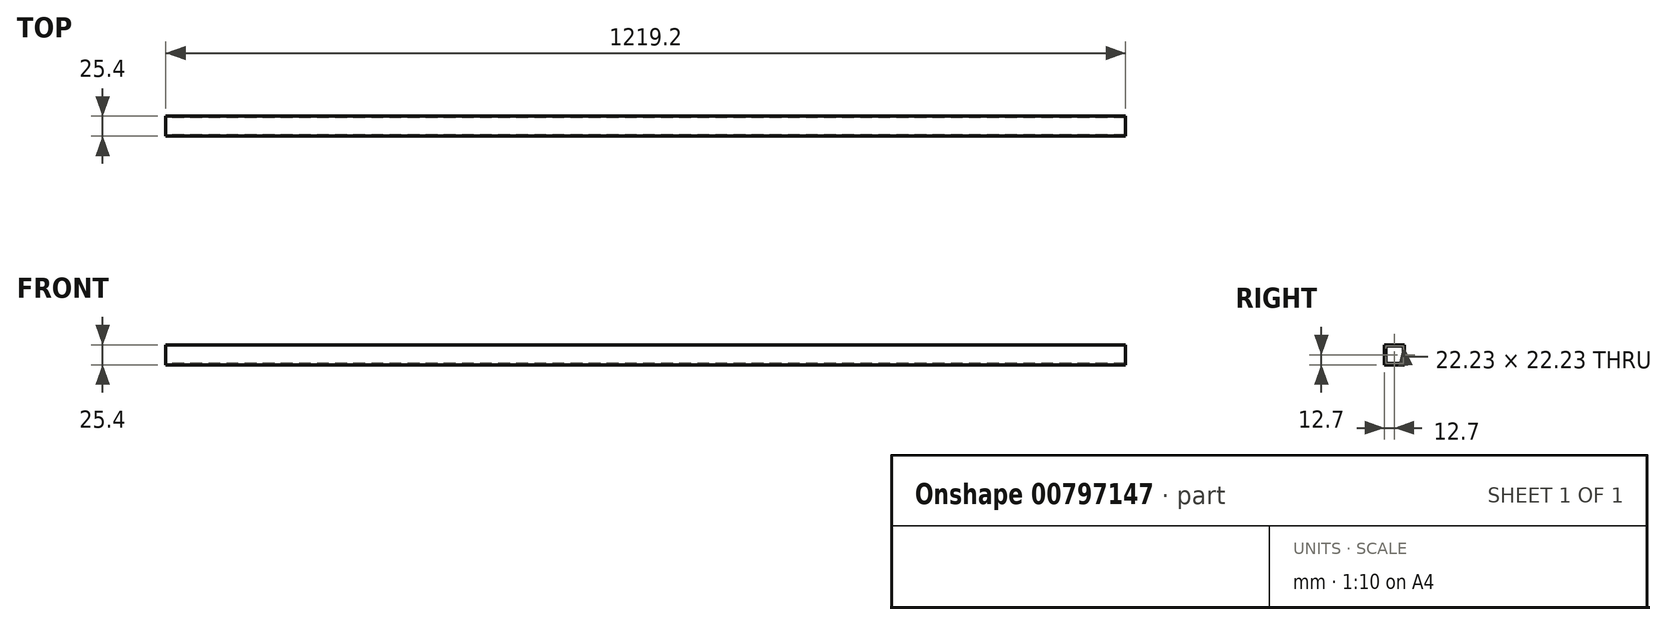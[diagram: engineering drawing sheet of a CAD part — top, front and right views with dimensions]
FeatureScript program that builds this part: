
annotation { "Feature Type Name" : "Feature", "Feature Type Description" : "" }
export const myFeature = defineFeature(function(context is Context, id is Id, definition is map)
    precondition{}
    {
        {
            var Q0;
            Q0=qCreatedBy(makeId("Right.planeOp"),FACE);
            var sketch = newSketch(context, id + "F0", { "sketchPlane" : qUnion([Q0])});
            skLineSegment(sketch, "E0.bottom", {"start": v(12.7, -12.7) * mm, "end": v(-12.7, -12.7) * mm});
            skLineSegment(sketch, "E0.top", {"start": v(12.7, 12.7) * mm, "end": v(-12.7, 12.7) * mm});
            skLineSegment(sketch, "E0.left", {"start": v(12.7, -12.7) * mm, "end": v(12.7, 12.7) * mm});
            skLineSegment(sketch, "E0.right", {"start": v(-12.7, -12.7) * mm, "end": v(-12.7, 12.7) * mm});
            skPoint(sketch, "E0.middle", {"position": v(0, 0) * mm});
            skLineSegment(sketch, "E1.0", {"start": v(11.11, 11.11) * mm, "end": v(-11.11, 11.11) * mm});
            skLineSegment(sketch, "E1.1", {"start": v(11.11, -11.11) * mm, "end": v(11.11, 11.11) * mm});
            skLineSegment(sketch, "E1.2", {"start": v(11.11, -11.11) * mm, "end": v(-11.11, -11.11) * mm});
            skLineSegment(sketch, "E1.3", {"start": v(-11.11, -11.11) * mm, "end": v(-11.11, 11.11) * mm});
            skSolve(sketch);
        }
        {
            var Q0;
            Q0=qSketchRegion(id+"F0",true);
            extrude(context, id + "F1", {"entities" : qUnion([Q0]), "depth" : 1219.2 * mm});
        }
    });
